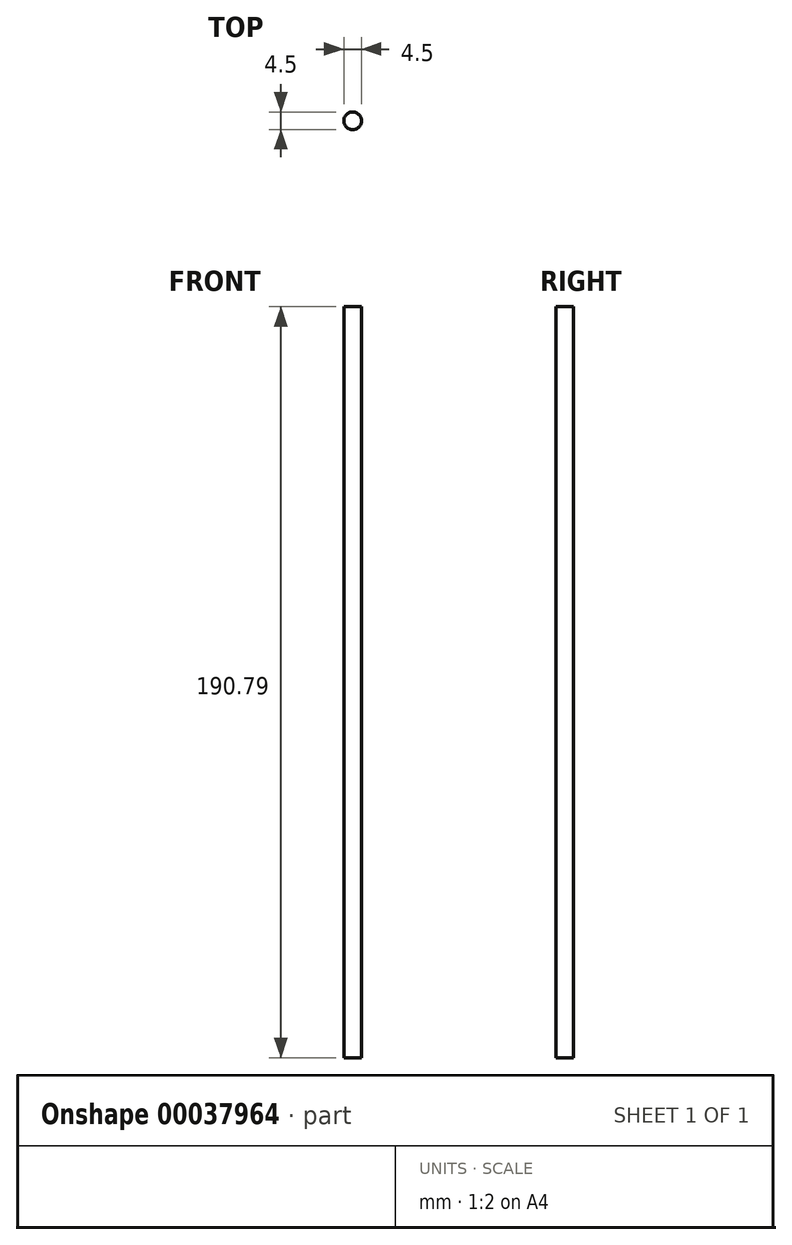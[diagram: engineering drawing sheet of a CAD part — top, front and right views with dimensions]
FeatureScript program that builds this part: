
annotation { "Feature Type Name" : "Feature", "Feature Type Description" : "" }
export const myFeature = defineFeature(function(context is Context, id is Id, definition is map)
    precondition{}
    {
        {
            var Q0;
            Q0=qCreatedBy(makeId("Top.planeOp"),FACE);
            var sketch = newSketch(context, id + "F0", { "sketchPlane" : qUnion([Q0])});
            skCircle(sketch, "E0", {"center": v(0, 0) * mm, "radius": 2.25 * mm});
            skSolve(sketch);
        }
        {
            var Q0;
            Q0=qSketchRegion(id+"F0",true);
            extrude(context, id + "F1", {"entities" : qUnion([Q0]), "depth" : 190.79 * mm});
        }
    });
